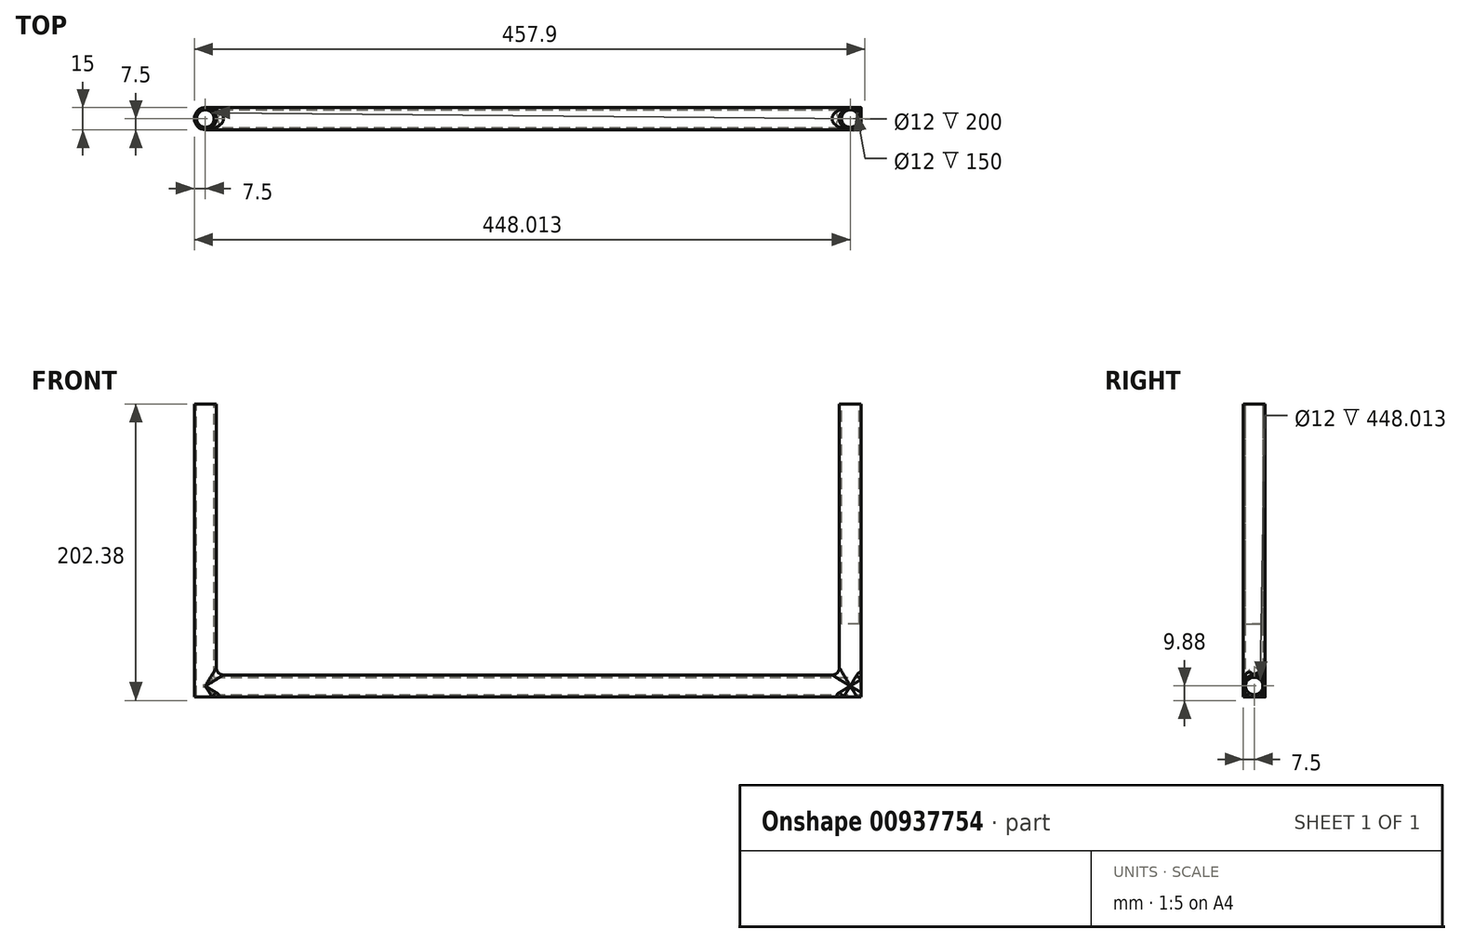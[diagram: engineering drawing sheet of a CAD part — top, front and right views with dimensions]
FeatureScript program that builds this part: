
annotation { "Feature Type Name" : "Feature", "Feature Type Description" : "" }
export const myFeature = defineFeature(function(context is Context, id is Id, definition is map)
    precondition{}
    {
        {
            var Q0;
            Q0=qCreatedBy(makeId("Top.planeOp"),FACE);
            var sketch = newSketch(context, id + "F0", { "sketchPlane" : qUnion([Q0])});
            skCircle(sketch, "E0", {"center": v(0, 0) * mm, "radius": 7.5 * mm});
            skSolve(sketch);
        }
        {
            var Q0;
            Q0=qSketchRegion(id+"F0",true);
            extrude(context, id + "F1", {"entities" : qUnion([Q0]), "depth" : 200 * mm, "offsetDistance" : 25 * mm});
        }
        {
            var Q0;
            Q0=makeQuery(id+"F1.opExtrude","CAP_FACE",FACE,{"disambiguationData":[OSD([sQuery(id+"F0.wireOp",EDGE,"E0")])],"isStart":false});
            var sketch = newSketch(context, id + "F2", { "sketchPlane" : qUnion([Q0])});
            skCircle(sketch, "E1", {"center": v(0, 0) * mm, "radius": 6 * mm});
            skSolve(sketch);
        }
        {
            var Q0;
            Q0=qSketchRegion(id+"F2",true);
            extrude(context, id + "F3", {"entities" : qUnion([Q0]), "operationType" : NewBodyOperationType.REMOVE, "oppositeDirection" : true, "depth" : 150 * mm, "offsetDistance" : 25 * mm});
        }
        {
            var Q0;
            Q0=qCreatedBy(makeId("Right.planeOp"),FACE);
            var sketch = newSketch(context, id + "F4", { "sketchPlane" : qUnion([Q0])});
            skCircle(sketch, "E2", {"center": v(0, 7.5) * mm, "radius": 7.5 * mm});
            skSolve(sketch);
        }
        {
            var Q0;
            Q0=qSketchRegion(id+"F4",true);
            extrude(context, id + "F5", {"entities" : qUnion([Q0]), "operationType" : NewBodyOperationType.ADD, "depth" : 448 * mm, "offsetDistance" : 25 * mm});
        }
        {
            var Q0;
            Q0=makeQuery(id+"F5.opExtrude","CAP_FACE",FACE,{"disambiguationData":[OSD([sQuery(id+"F4.wireOp",EDGE,"E2")])],"isStart":false});
            var sketch = newSketch(context, id + "F6", { "sketchPlane" : qUnion([Q0])});
            skCircle(sketch, "E3", {"center": v(0, 7.5) * mm, "radius": 6 * mm});
            skSolve(sketch);
        }
        {
            var Q0;
            Q0=qSketchRegion(id+"F6",true);
            extrude(context, id + "F7", {"entities" : qUnion([Q0]), "operationType" : NewBodyOperationType.REMOVE, "oppositeDirection" : true, "depth" : 448 * mm, "offsetDistance" : 25 * mm});
        }
        {
            var Q0;
            Q0=qCreatedBy(makeId("Top.planeOp"),FACE);
            var sketch = newSketch(context, id + "F8", { "sketchPlane" : qUnion([Q0])});
            skCircle(sketch, "E4", {"center": v(0, 0) * mm, "radius": 6 * mm});
            skSolve(sketch);
        }
        {
            var Q0;
            Q0=qSketchRegion(id+"F8",true);
            extrude(context, id + "F9", {"entities" : qUnion([Q0]), "operationType" : NewBodyOperationType.REMOVE, "depth" : 500 * mm, "offsetDistance" : 25 * mm});
        }
        {
            var Q0;
            Q0=qCreatedBy(makeId("Top.planeOp"),FACE);
            var sketch = newSketch(context, id + "F10", { "sketchPlane" : qUnion([Q0])});
            skCircle(sketch, "E5", {"center": v(440.51, 0) * mm, "radius": 7.5 * mm});
            skSolve(sketch);
        }
        {
            var Q0;
            Q0=qSketchRegion(id+"F10",true);
            extrude(context, id + "F11", {"entities" : qUnion([Q0]), "operationType" : NewBodyOperationType.ADD, "depth" : 200 * mm, "offsetDistance" : 25 * mm});
        }
        {
            var Q0;
            Q0=makeQuery(id+"F11.opExtrude","CAP_FACE",FACE,{"disambiguationData":[OSD([sQuery(id+"F10.wireOp",EDGE,"E5")])],"isStart":false});
            var sketch = newSketch(context, id + "F12", { "sketchPlane" : qUnion([Q0])});
            skCircle(sketch, "E6", {"center": v(440.51, 0) * mm, "radius": 6 * mm});
            skSolve(sketch);
        }
        {
            var Q0;
            Q0=qSketchRegion(id+"F12",true);
            extrude(context, id + "F13", {"entities" : qUnion([Q0]), "operationType" : NewBodyOperationType.REMOVE, "oppositeDirection" : true, "depth" : 150 * mm, "offsetDistance" : 25 * mm});
        }
        {
            var Q0;
            Q0=makeQuery(id+"F5.opExtrude","CAP_FACE",FACE,{"disambiguationData":[OSD([sQuery(id+"F4.wireOp",EDGE,"E2")])],"isStart":false});
            var sketch = newSketch(context, id + "F14", { "sketchPlane" : qUnion([Q0])});
            skCircle(sketch, "E7", {"center": v(0, 7.5) * mm, "radius": 6 * mm});
            skSolve(sketch);
        }
        {
            var Q0;
            Q0=qSketchRegion(id+"F14",true);
            extrude(context, id + "F15", {"entities" : qUnion([Q0]), "operationType" : NewBodyOperationType.REMOVE, "oppositeDirection" : true, "depth" : 449 * mm, "offsetDistance" : 25 * mm});
        }
        {
            var Q0;
            Q0=makeQuery(id+"F5.boolean.opBoolean","INTERSECT",EDGE,{"disambiguationData":[OD(0.0)],"derivedFrom":[makeQuery(id+"F1.opExtrude","SWEPT_FACE",FACE,{"disambiguationData":[OSD([sQuery(id+"F0.wireOp",EDGE,"E0")])]}),makeQuery(id+"F5.opExtrude","SWEPT_FACE",FACE,{"disambiguationData":[OSD([sQuery(id+"F4.wireOp",EDGE,"E2")])]})]});
            var Q1;
            Q1=makeQuery(id+"F5.boolean.opBoolean","INTERSECT",EDGE,{"disambiguationData":[OD(1.0)],"derivedFrom":[makeQuery(id+"F1.opExtrude","SWEPT_FACE",FACE,{"disambiguationData":[OSD([sQuery(id+"F0.wireOp",EDGE,"E0")])]}),makeQuery(id+"F5.opExtrude","SWEPT_FACE",FACE,{"disambiguationData":[OSD([sQuery(id+"F4.wireOp",EDGE,"E2")])]})]});
            var Q2;
            {var subQ0=sQuery(id+"F0.wireOp",EDGE,"E0");var subQ1=sQuery(id+"F4.wireOp",EDGE,"E2");Q2=makeQuery(id+"F11.boolean.opBoolean","INTERSECT",EDGE,{"disambiguationData":[OD(1.0)],"derivedFrom":[makeQuery(id+"F5.boolean.opBoolean","SPLIT",FACE,{"disambiguationData":[TD([makeQuery(id+"F1.opExtrude","SWEPT_FACE",FACE,{"disambiguationData":[OSD([subQ0])]}),makeQuery(id+"F1.opExtrude","CAP_FACE",FACE,{"disambiguationData":[OSD([subQ0])],"isStart":true}),makeQuery(id+"F5.opExtrude","CAP_FACE",FACE,{"disambiguationData":[OSD([subQ1])],"isStart":false})])],"derivedFrom":makeQuery(id+"F5.opExtrude","SWEPT_FACE",FACE,{"disambiguationData":[OSD([subQ1])]})}),makeQuery(id+"F11.opExtrude","SWEPT_FACE",FACE,{"disambiguationData":[OSD([sQuery(id+"F10.wireOp",EDGE,"E5")])]})]});}
            var Q3;
            {var subQ0=sQuery(id+"F0.wireOp",EDGE,"E0");var subQ1=sQuery(id+"F4.wireOp",EDGE,"E2");Q3=makeQuery(id+"F11.boolean.opBoolean","INTERSECT",EDGE,{"disambiguationData":[OD(0.0)],"derivedFrom":[makeQuery(id+"F5.boolean.opBoolean","SPLIT",FACE,{"disambiguationData":[TD([makeQuery(id+"F1.opExtrude","SWEPT_FACE",FACE,{"disambiguationData":[OSD([subQ0])]}),makeQuery(id+"F1.opExtrude","CAP_FACE",FACE,{"disambiguationData":[OSD([subQ0])],"isStart":true}),makeQuery(id+"F5.opExtrude","CAP_FACE",FACE,{"disambiguationData":[OSD([subQ1])],"isStart":false})])],"derivedFrom":makeQuery(id+"F5.opExtrude","SWEPT_FACE",FACE,{"disambiguationData":[OSD([subQ1])]})}),makeQuery(id+"F11.opExtrude","SWEPT_FACE",FACE,{"disambiguationData":[OSD([sQuery(id+"F10.wireOp",EDGE,"E5")])]})]});}
            var Q4;
            {var subQ0=sQuery(id+"F0.wireOp",EDGE,"E0");var subQ1=sQuery(id+"F4.wireOp",EDGE,"E2");Q4=makeQuery(id+"F11.boolean.opBoolean","INTERSECT",EDGE,{"disambiguationData":[OD(5.0)],"derivedFrom":[makeQuery(id+"F5.boolean.opBoolean","SPLIT",FACE,{"disambiguationData":[TD([makeQuery(id+"F1.opExtrude","SWEPT_FACE",FACE,{"disambiguationData":[OSD([subQ0])]}),makeQuery(id+"F1.opExtrude","CAP_FACE",FACE,{"disambiguationData":[OSD([subQ0])],"isStart":true}),makeQuery(id+"F5.opExtrude","CAP_FACE",FACE,{"disambiguationData":[OSD([subQ1])],"isStart":false})])],"derivedFrom":makeQuery(id+"F5.opExtrude","SWEPT_FACE",FACE,{"disambiguationData":[OSD([subQ1])]})}),makeQuery(id+"F11.opExtrude","SWEPT_FACE",FACE,{"disambiguationData":[OSD([sQuery(id+"F10.wireOp",EDGE,"E5")])]})]});}
            var Q5;
            {var subQ0=sQuery(id+"F0.wireOp",EDGE,"E0");var subQ1=sQuery(id+"F4.wireOp",EDGE,"E2");Q5=makeQuery(id+"F11.boolean.opBoolean","INTERSECT",EDGE,{"disambiguationData":[OD(3.0)],"derivedFrom":[makeQuery(id+"F5.boolean.opBoolean","SPLIT",FACE,{"disambiguationData":[TD([makeQuery(id+"F1.opExtrude","SWEPT_FACE",FACE,{"disambiguationData":[OSD([subQ0])]}),makeQuery(id+"F1.opExtrude","CAP_FACE",FACE,{"disambiguationData":[OSD([subQ0])],"isStart":true}),makeQuery(id+"F5.opExtrude","CAP_FACE",FACE,{"disambiguationData":[OSD([subQ1])],"isStart":false})])],"derivedFrom":makeQuery(id+"F5.opExtrude","SWEPT_FACE",FACE,{"disambiguationData":[OSD([subQ1])]})}),makeQuery(id+"F11.opExtrude","SWEPT_FACE",FACE,{"disambiguationData":[OSD([sQuery(id+"F10.wireOp",EDGE,"E5")])]})]});}
            fillet(context, id + "F16", {"entities" : qUnion([Q0, Q1, Q2, Q3, Q4, Q5]), "radius" : 5 * mm, "tangentPropagation" : true, "allowEdgeOverflow" : false});
        }
    });
